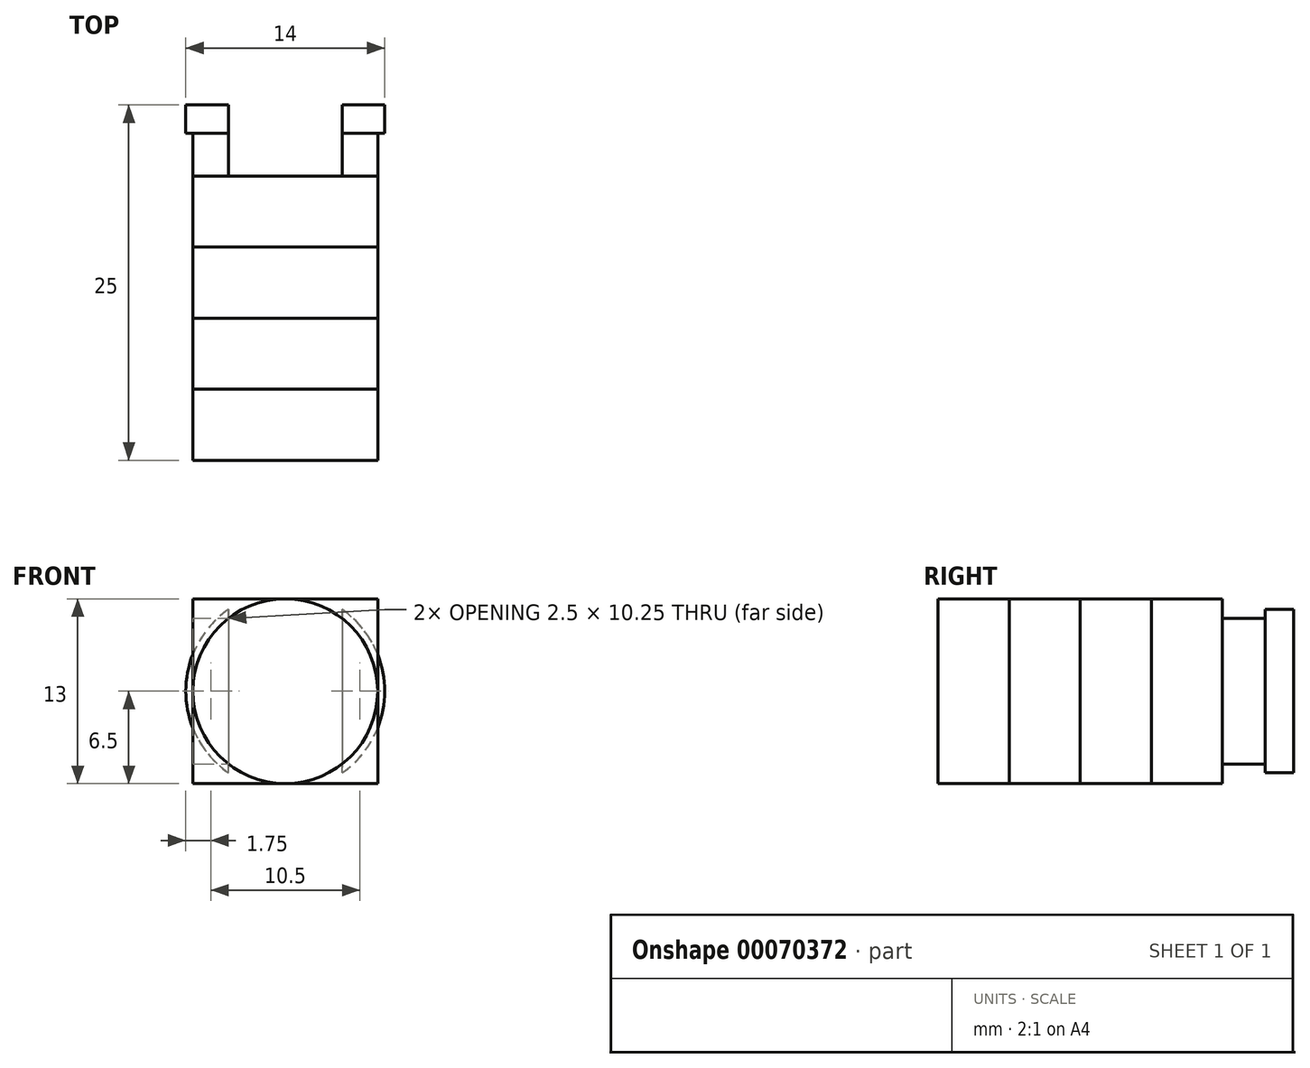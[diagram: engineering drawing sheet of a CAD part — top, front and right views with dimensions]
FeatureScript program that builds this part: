
annotation { "Feature Type Name" : "Feature", "Feature Type Description" : "" }
export const myFeature = defineFeature(function(context is Context, id is Id, definition is map)
    precondition{}
    {
        {
            var Q0;
            Q0=qCreatedBy(makeId("Front.planeOp"),FACE);
            var sketch = newSketch(context, id + "F0", { "sketchPlane" : qUnion([Q0])});
            skCircle(sketch, "E0", {"center": v(0, 0) * mm, "radius": 6.5 * mm});
            skLineSegment(sketch, "E1.rect.bottom", {"start": v(-4, 9.84) * mm, "end": v(4, 9.84) * mm});
            skLineSegment(sketch, "E1.rect.top", {"start": v(-4, -9.84) * mm, "end": v(4, -9.84) * mm});
            skLineSegment(sketch, "E1.rect.left", {"start": v(-4, 9.84) * mm, "end": v(-4, -9.84) * mm});
            skLineSegment(sketch, "E1.rect.right", {"start": v(4, 9.84) * mm, "end": v(4, -9.84) * mm});
            skLineSegment(sketch, "E2", {"start": v(11.65, 0) * mm, "end": v(-11.24, 0) * mm, "construction": true});
            skLineSegment(sketch, "E3", {"start": v(0, -11.93) * mm, "end": v(0, 15.17) * mm, "construction": true});
            skLineSegment(sketch, "E4.rect.bottom", {"start": v(-6.5, -6.5) * mm, "end": v(6.5, -6.5) * mm});
            skLineSegment(sketch, "E4.rect.top", {"start": v(-6.5, 6.5) * mm, "end": v(6.5, 6.5) * mm});
            skLineSegment(sketch, "E4.rect.left", {"start": v(-6.5, -6.5) * mm, "end": v(-6.5, 6.5) * mm});
            skLineSegment(sketch, "E4.rect.right", {"start": v(6.5, -6.5) * mm, "end": v(6.5, 6.5) * mm});
            skSolve(sketch);
        }
        {
            var Q0;
            {var subQ0=sQuery(id+"F0.wireOp",EDGE,"E1.rect.right");var subQ1=sQuery(id+"F0.wireOp",EDGE,"E0");var subQ2=makeQuery(id+"F0.imprint","INTERSECT",VERTEX,{"disambiguationData":[OD(0.0)],"derivedFrom":[subQ1,subQ0]});Q0=makeQuery(id+"F0.imprint","IMPRINT",FACE,{"disambiguationData":[TD([[makeQuery(id+"F0.imprint","IMPRINT",EDGE,{"disambiguationData":[TD([[subQ2,1.0]])],"derivedFrom":subQ1}),1.0]])]});}
            var Q1;
            {var subQ0=sQuery(id+"F0.wireOp",EDGE,"E1.rect.left");var subQ1=sQuery(id+"F0.wireOp",EDGE,"E0");var subQ2=makeQuery(id+"F0.imprint","INTERSECT",VERTEX,{"disambiguationData":[OD(0.0)],"derivedFrom":[subQ1,subQ0]});Q1=makeQuery(id+"F0.imprint","IMPRINT",FACE,{"disambiguationData":[TD([[makeQuery(id+"F0.imprint","IMPRINT",EDGE,{"disambiguationData":[TD([[subQ2,-1.0]])],"derivedFrom":subQ1}),1.0]])]});}
            extrude(context, id + "F1", {"entities" : qUnion([Q0, Q1]), "depth" : 5 * mm});
        }
        {
            var Q0;
            {var subQ0=sQuery(id+"F0.wireOp",EDGE,"E0");var subQ2=sQuery(id+"F0.wireOp",EDGE,"E1.rect.right");var subQ4=makeQuery(id+"F0.imprint","INTERSECT",VERTEX,{"disambiguationData":[OD(0.0)],"derivedFrom":[subQ0,subQ2]});Q0=makeQuery(id+"F0.imprint","IMPRINT",FACE,{"disambiguationData":[TD([[makeQuery(id+"F0.imprint","IMPRINT",EDGE,{"disambiguationData":[TD([[subQ4,-1.0]])],"derivedFrom":subQ0}),1.0]])]});}
            var Q1;
            {var subQ0=sQuery(id+"F0.wireOp",EDGE,"E1.rect.right");var subQ1=sQuery(id+"F0.wireOp",EDGE,"E0");var subQ2=makeQuery(id+"F0.imprint","INTERSECT",VERTEX,{"disambiguationData":[OD(0.0)],"derivedFrom":[subQ1,subQ0]});Q1=makeQuery(id+"F0.imprint","IMPRINT",FACE,{"disambiguationData":[TD([[makeQuery(id+"F0.imprint","IMPRINT",EDGE,{"disambiguationData":[TD([[subQ2,-1.0]])],"derivedFrom":subQ1}),-1.0]])]});}
            var Q2;
            {var subQ1=sQuery(id+"F0.wireOp",EDGE,"E1.rect.bottom");Q2=makeQuery(id+"F0.imprint","IMPRINT",FACE,{"disambiguationData":[TD([[makeQuery(id+"F0.imprint","IMPRINT",EDGE,{"derivedFrom":subQ1}),-1.0]])]});}
            var Q3;
            {var subQ0=sQuery(id+"F0.wireOp",EDGE,"E4.rect.top");var subQ1=sQuery(id+"F0.wireOp",EDGE,"E0");var subQ2=makeQuery(id+"F0.imprint","INTERSECT",VERTEX,{"derivedFrom":[subQ1,subQ0]});Q3=makeQuery(id+"F0.imprint","IMPRINT",FACE,{"disambiguationData":[TD([[makeQuery(id+"F0.imprint","IMPRINT",EDGE,{"disambiguationData":[TD([[subQ2,-1.0]])],"derivedFrom":subQ1}),-1.0]])]});}
            var Q4;
            {var subQ0=sQuery(id+"F0.wireOp",EDGE,"E1.rect.left");var subQ1=sQuery(id+"F0.wireOp",EDGE,"E0");var subQ2=makeQuery(id+"F0.imprint","INTERSECT",VERTEX,{"disambiguationData":[OD(1.0)],"derivedFrom":[subQ1,subQ0]});Q4=makeQuery(id+"F0.imprint","IMPRINT",FACE,{"disambiguationData":[TD([[makeQuery(id+"F0.imprint","IMPRINT",EDGE,{"disambiguationData":[TD([[subQ2,-1.0]])],"derivedFrom":subQ1}),-1.0]])]});}
            var Q5;
            {var subQ0=sQuery(id+"F0.wireOp",EDGE,"E4.rect.bottom");var subQ1=sQuery(id+"F0.wireOp",EDGE,"E0");var subQ2=makeQuery(id+"F0.imprint","INTERSECT",VERTEX,{"derivedFrom":[subQ1,subQ0]});Q5=makeQuery(id+"F0.imprint","IMPRINT",FACE,{"disambiguationData":[TD([[makeQuery(id+"F0.imprint","IMPRINT",EDGE,{"disambiguationData":[TD([[subQ2,-1.0]])],"derivedFrom":subQ1}),-1.0]])]});}
            var Q6;
            {var subQ5=sQuery(id+"F0.wireOp",EDGE,"E1.rect.top");Q6=makeQuery(id+"F0.imprint","IMPRINT",FACE,{"disambiguationData":[TD([[makeQuery(id+"F0.imprint","IMPRINT",EDGE,{"derivedFrom":subQ5}),1.0]])]});}
            var Q7;
            Q7 = qSketchRegion(id + "F4", true);
            extrude(context, id + "F2", {"entities" : qUnion([Q0, Q1, Q2, Q3, Q4, Q5, Q6, Q7]), "operationType" : NewBodyOperationType.REMOVE, "depth" : 30 * mm});
        }
        {
            var Q0;
            Q0=makeQuery(id+"F1.opExtrude","CAP_FACE",FACE,{"disambiguationData":[OSD([sQuery(id+"F0.wireOp",EDGE,"E0"),sQuery(id+"F0.wireOp",EDGE,"E1.rect.left")])],"isStart":false});
            cPlane(context, id + "F3", {"entities" : qUnion([Q0]), "cplaneType" : CPlaneType.OFFSET, "offset" : 0 * mm, "width" : 150 * mm, "height" : 150 * mm});
        }
        {
            var Q0;
            Q0=qCreatedBy(id+"F3.planeOp",FACE);
            var sketch = newSketch(context, id + "F4", { "sketchPlane" : qUnion([Q0])});
            skLineSegment(sketch, "E5.rect.bottom", {"start": v(-6.5, -6.5) * mm, "end": v(6.5, -6.5) * mm});
            skLineSegment(sketch, "E5.rect.top", {"start": v(-6.5, 6.5) * mm, "end": v(6.5, 6.5) * mm});
            skLineSegment(sketch, "E5.rect.left", {"start": v(-6.5, -6.5) * mm, "end": v(-6.5, 6.5) * mm});
            skLineSegment(sketch, "E5.rect.right", {"start": v(6.5, -6.5) * mm, "end": v(6.5, 6.5) * mm});
            skPoint(sketch, "E5.rect.middle", {"position": v(0, 0) * mm});
            skCircle(sketch, "E6", {"center": v(0, 0) * mm, "radius": 6.5 * mm});
            skLineSegment(sketch, "E7", {"start": v(-8.74, 0) * mm, "end": v(9.18, 0) * mm, "construction": true});
            skLineSegment(sketch, "E8", {"start": v(0, 9.31) * mm, "end": v(0, -14.04) * mm, "construction": true});
            skSolve(sketch);
        }
        {
            var Q0;
            {var subQ0=sQuery(id+"F4.wireOp",EDGE,"E5.rect.bottom");Q0=makeQuery(id+"F4.imprint","IMPRINT",FACE,{"disambiguationData":[TD([[makeQuery(id+"F4.imprint","IMPRINT",EDGE,{"derivedFrom":subQ0}),1.0]])]});}
            var Q1;
            {var subQ0=sQuery(id+"F4.wireOp",EDGE,"E5.rect.top");Q1=makeQuery(id+"F4.imprint","IMPRINT",FACE,{"disambiguationData":[TD([[makeQuery(id+"F4.imprint","IMPRINT",EDGE,{"derivedFrom":subQ0}),-1.0]])]});}
            extrude(context, id + "F5", {"entities" : qUnion([Q0, Q1]), "operationType" : NewBodyOperationType.ADD, "depth" : 5 * mm});
        }
        {
            var Q0;
            {var subQ0=sQuery(id+"F4.wireOp",EDGE,"E6");var subQ1=makeQuery(id+"F4.imprint","INTERSECT",VERTEX,{"derivedFrom":[sQuery(id+"F4.wireOp",EDGE,"E5.rect.top"),subQ0]});Q0=makeQuery(id+"F4.imprint","IMPRINT",FACE,{"disambiguationData":[TD([[makeQuery(id+"F4.imprint","IMPRINT",EDGE,{"disambiguationData":[TD([[subQ1,1.0]])],"derivedFrom":subQ0}),1.0]])]});}
            extrude(context, id + "F6", {"entities" : qUnion([Q0]), "operationType" : NewBodyOperationType.ADD, "depth" : 10 * mm});
        }
        {
            var Q0;
            Q0=makeQuery(id+"F6.opExtrude","CAP_FACE",FACE,{"disambiguationData":[OSD([sQuery(id+"F4.wireOp",EDGE,"E5.rect.left"),sQuery(id+"F4.wireOp",EDGE,"E5.rect.right"),sQuery(id+"F4.wireOp",EDGE,"E6")])],"isStart":false});
            cPlane(context, id + "F7", {"entities" : qUnion([Q0]), "cplaneType" : CPlaneType.OFFSET, "offset" : 0 * mm, "width" : 150 * mm, "height" : 150 * mm});
        }
        {
            var Q0;
            Q0=qCreatedBy(id+"F7.planeOp",FACE);
            var sketch = newSketch(context, id + "F8", { "sketchPlane" : qUnion([Q0])});
            skCircle(sketch, "E9", {"center": v(0, 0) * mm, "radius": 6.5 * mm});
            skLineSegment(sketch, "E10.rect.bottom", {"start": v(-6.5, 6.5) * mm, "end": v(6.5, 6.5) * mm});
            skLineSegment(sketch, "E10.rect.top", {"start": v(-6.5, -6.5) * mm, "end": v(6.5, -6.5) * mm});
            skLineSegment(sketch, "E10.rect.left", {"start": v(-6.5, 6.5) * mm, "end": v(-6.5, -6.5) * mm});
            skLineSegment(sketch, "E10.rect.right", {"start": v(6.5, 6.5) * mm, "end": v(6.5, -6.5) * mm});
            skSolve(sketch);
        }
        {
            var Q0;
            {var subQ0=sQuery(id+"F8.wireOp",EDGE,"E10.rect.bottom");var subQ1=sQuery(id+"F8.wireOp",EDGE,"E9");var subQ2=makeQuery(id+"F8.imprint","INTERSECT",VERTEX,{"derivedFrom":[subQ1,subQ0]});Q0=makeQuery(id+"F8.imprint","IMPRINT",FACE,{"disambiguationData":[TD([[makeQuery(id+"F8.imprint","IMPRINT",EDGE,{"disambiguationData":[TD([[subQ2,-1.0]])],"derivedFrom":subQ1}),-1.0]])]});}
            var Q1;
            {var subQ0=sQuery(id+"F8.wireOp",EDGE,"E10.rect.bottom");var subQ1=sQuery(id+"F8.wireOp",EDGE,"E9");var subQ2=makeQuery(id+"F8.imprint","INTERSECT",VERTEX,{"derivedFrom":[subQ1,subQ0]});Q1=makeQuery(id+"F8.imprint","IMPRINT",FACE,{"disambiguationData":[TD([[makeQuery(id+"F8.imprint","IMPRINT",EDGE,{"disambiguationData":[TD([[subQ2,1.0]])],"derivedFrom":subQ1}),-1.0]])]});}
            var Q2;
            {var subQ0=sQuery(id+"F8.wireOp",EDGE,"E10.rect.right");var subQ1=sQuery(id+"F8.wireOp",EDGE,"E9");var subQ2=makeQuery(id+"F8.imprint","INTERSECT",VERTEX,{"derivedFrom":[subQ1,subQ0]});Q2=makeQuery(id+"F8.imprint","IMPRINT",FACE,{"disambiguationData":[TD([[makeQuery(id+"F8.imprint","IMPRINT",EDGE,{"disambiguationData":[TD([[subQ2,1.0]])],"derivedFrom":subQ1}),-1.0]])]});}
            var Q3;
            {var subQ0=sQuery(id+"F8.wireOp",EDGE,"E10.rect.left");var subQ1=sQuery(id+"F8.wireOp",EDGE,"E9");var subQ2=makeQuery(id+"F8.imprint","INTERSECT",VERTEX,{"derivedFrom":[subQ1,subQ0]});Q3=makeQuery(id+"F8.imprint","IMPRINT",FACE,{"disambiguationData":[TD([[makeQuery(id+"F8.imprint","IMPRINT",EDGE,{"disambiguationData":[TD([[subQ2,-1.0]])],"derivedFrom":subQ1}),-1.0]])]});}
            extrude(context, id + "F9", {"entities" : qUnion([Q0, Q1, Q2, Q3]), "operationType" : NewBodyOperationType.ADD, "depth" : 5 * mm});
        }
        {
            var Q0;
            {var subQ0=sQuery(id+"F8.wireOp",EDGE,"E9");var subQ1=makeQuery(id+"F8.imprint","INTERSECT",VERTEX,{"derivedFrom":[subQ0,sQuery(id+"F8.wireOp",EDGE,"E10.rect.bottom")]});Q0=makeQuery(id+"F8.imprint","IMPRINT",FACE,{"disambiguationData":[TD([[makeQuery(id+"F8.imprint","IMPRINT",EDGE,{"disambiguationData":[TD([[subQ1,1.0]])],"derivedFrom":subQ0}),1.0]])]});}
            extrude(context, id + "F10", {"entities" : qUnion([Q0]), "operationType" : NewBodyOperationType.ADD, "depth" : 10 * mm});
        }
        {
            var Q0;
            {var subQ0=sQuery(id+"F0.wireOp",EDGE,"E0");var subQ1=makeQuery(id+"F0.imprint","INTERSECT",VERTEX,{"derivedFrom":[subQ0,sQuery(id+"F0.wireOp",EDGE,"E4.rect.right")]});Q0=makeQuery(id+"F0.imprint","IMPRINT",FACE,{"disambiguationData":[TD([[makeQuery(id+"F0.imprint","IMPRINT",EDGE,{"disambiguationData":[TD([[subQ1,-1.0]])],"derivedFrom":subQ0}),1.0]])]});}
            cPlane(context, id + "F11", {"entities" : qUnion([Q0]), "cplaneType" : CPlaneType.OFFSET, "offset" : 0 * mm, "width" : 150 * mm, "height" : 150 * mm});
        }
        {
            var Q0;
            Q0=qCreatedBy(id+"F11.planeOp",FACE);
            var sketch = newSketch(context, id + "F12", { "sketchPlane" : qUnion([Q0])});
            skCircle(sketch, "E11", {"center": v(0, 0) * mm, "radius": 7 * mm});
            skCircle(sketch, "E12", {"center": v(0, 0) * mm, "radius": 6.5 * mm});
            skLineSegment(sketch, "E13.rect.bottom", {"start": v(-4, 11.58) * mm, "end": v(4, 11.58) * mm});
            skLineSegment(sketch, "E13.rect.top", {"start": v(-4, -11.58) * mm, "end": v(4, -11.58) * mm});
            skLineSegment(sketch, "E13.rect.left", {"start": v(-4, 11.58) * mm, "end": v(-4, -11.58) * mm});
            skLineSegment(sketch, "E13.rect.right", {"start": v(4, 11.58) * mm, "end": v(4, -11.58) * mm});
            skSolve(sketch);
        }
        {
            var Q0;
            Q0=makeQuery(id+"F12.imprint","IMPRINT",FACE,{"disambiguationData":[TD([[makeQuery(id+"F12.imprint","IMPRINT",EDGE,{"derivedFrom":sQuery(id+"F12.wireOp",EDGE,"E11")}),1.0]])]});
            extrude(context, id + "F13", {"entities" : qUnion([Q0]), "operationType" : NewBodyOperationType.ADD, "depth" : 2 * mm});
        }
        {
            var Q0;
            {var subQ5=sQuery(id+"F12.wireOp",EDGE,"E13.rect.bottom");Q0=makeQuery(id+"F12.imprint","IMPRINT",FACE,{"disambiguationData":[TD([[makeQuery(id+"F12.imprint","IMPRINT",EDGE,{"derivedFrom":subQ5}),-1.0]])]});}
            var Q1;
            {var subQ5=sQuery(id+"F12.wireOp",EDGE,"E13.rect.top");Q1=makeQuery(id+"F12.imprint","IMPRINT",FACE,{"disambiguationData":[TD([[makeQuery(id+"F12.imprint","IMPRINT",EDGE,{"derivedFrom":subQ5}),1.0]])]});}
            var Q2;
            {var subQ0=sQuery(id+"F12.wireOp",EDGE,"E13.rect.left");var subQ1=sQuery(id+"F12.wireOp",EDGE,"E11");var subQ2=makeQuery(id+"F12.imprint","INTERSECT",VERTEX,{"disambiguationData":[OD(0.0)],"derivedFrom":[subQ1,subQ0]});Q2=makeQuery(id+"F12.imprint","IMPRINT",FACE,{"disambiguationData":[TD([[makeQuery(id+"F12.imprint","IMPRINT",EDGE,{"disambiguationData":[TD([[subQ2,1.0]])],"derivedFrom":subQ1}),1.0]])]});}
            var Q3;
            {var subQ0=sQuery(id+"F12.wireOp",EDGE,"E13.rect.left");var subQ1=sQuery(id+"F12.wireOp",EDGE,"E11");var subQ2=makeQuery(id+"F12.imprint","INTERSECT",VERTEX,{"disambiguationData":[OD(1.0)],"derivedFrom":[subQ1,subQ0]});Q3=makeQuery(id+"F12.imprint","IMPRINT",FACE,{"disambiguationData":[TD([[makeQuery(id+"F12.imprint","IMPRINT",EDGE,{"disambiguationData":[TD([[subQ2,-1.0]])],"derivedFrom":subQ1}),1.0]])]});}
            extrude(context, id + "F14", {"entities" : qUnion([Q0, Q1, Q2, Q3]), "operationType" : NewBodyOperationType.REMOVE, "depth" : 3 * mm});
        }
        {
            var Q0;
            Q0=makeQuery(id+"F1.opExtrude","SWEPT_BODY",BODY,{"disambiguationData":[OSD([sQuery(id+"F0.wireOp",EDGE,"E0"),sQuery(id+"F0.wireOp",EDGE,"E1.rect.right")])]});
            transform(context, id + "F15", {"entities" : qUnion([Q0]), "transformType" : TransformType.TRANSLATION_3D, "dx" : 0 * mm, "dy" : 0 * mm, "dz" : 0 * mm, "makeCopy" : true});
        }
    });
